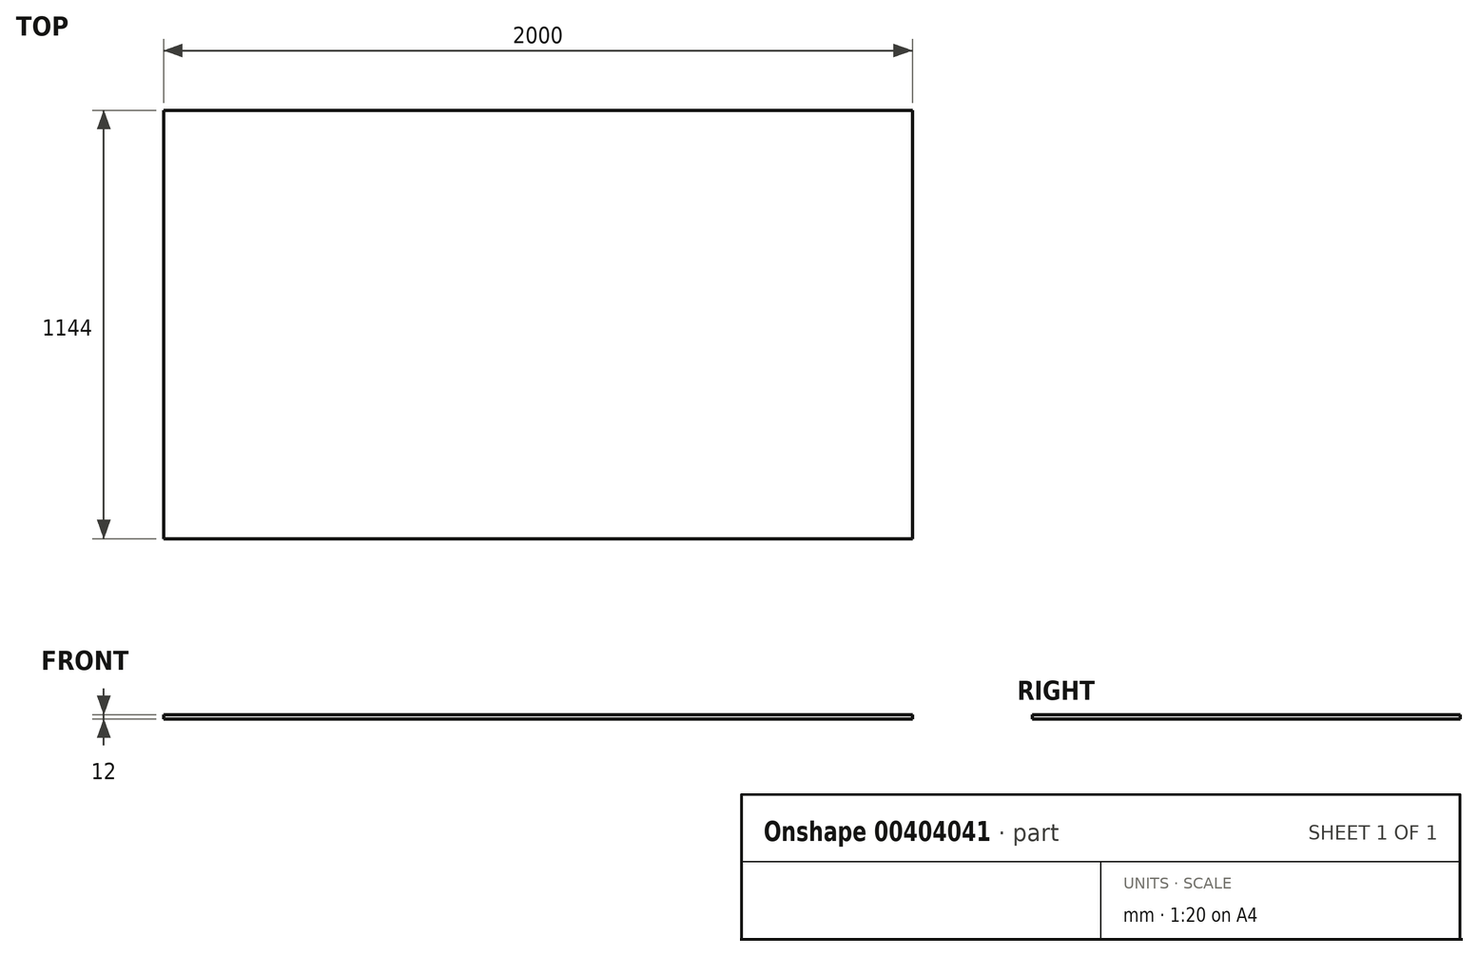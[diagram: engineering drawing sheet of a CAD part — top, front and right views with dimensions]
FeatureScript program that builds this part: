
annotation { "Feature Type Name" : "Feature", "Feature Type Description" : "" }
export const myFeature = defineFeature(function(context is Context, id is Id, definition is map)
    precondition{}
    {
        {
            var Q0;
            Q0=qCreatedBy(makeId("Top.planeOp"),FACE);
            var sketch = newSketch(context, id + "F0", { "sketchPlane" : qUnion([Q0])});
            skLineSegment(sketch, "E0.bottom", {"start": v(0, 0) * mm, "end": v(2000, 0) * mm});
            skLineSegment(sketch, "E0.top", {"start": v(0, 1144) * mm, "end": v(2000, 1144) * mm});
            skLineSegment(sketch, "E0.left", {"start": v(0, 0) * mm, "end": v(0, 1144) * mm});
            skLineSegment(sketch, "E0.right", {"start": v(2000, 0) * mm, "end": v(2000, 1144) * mm});
            skSolve(sketch);
        }
        {
            var Q0;
            Q0=makeQuery(id+"F0.imprint","IMPRINT",FACE,{"disambiguationData":[TD([[makeQuery(id+"F0.imprint","IMPRINT",EDGE,{"derivedFrom":sQuery(id+"F0.wireOp",EDGE,"E0.bottom")}),1.0]])]});
            extrude(context, id + "F1", {"entities" : qUnion([Q0]), "depth" : 12 * mm});
        }
    });
